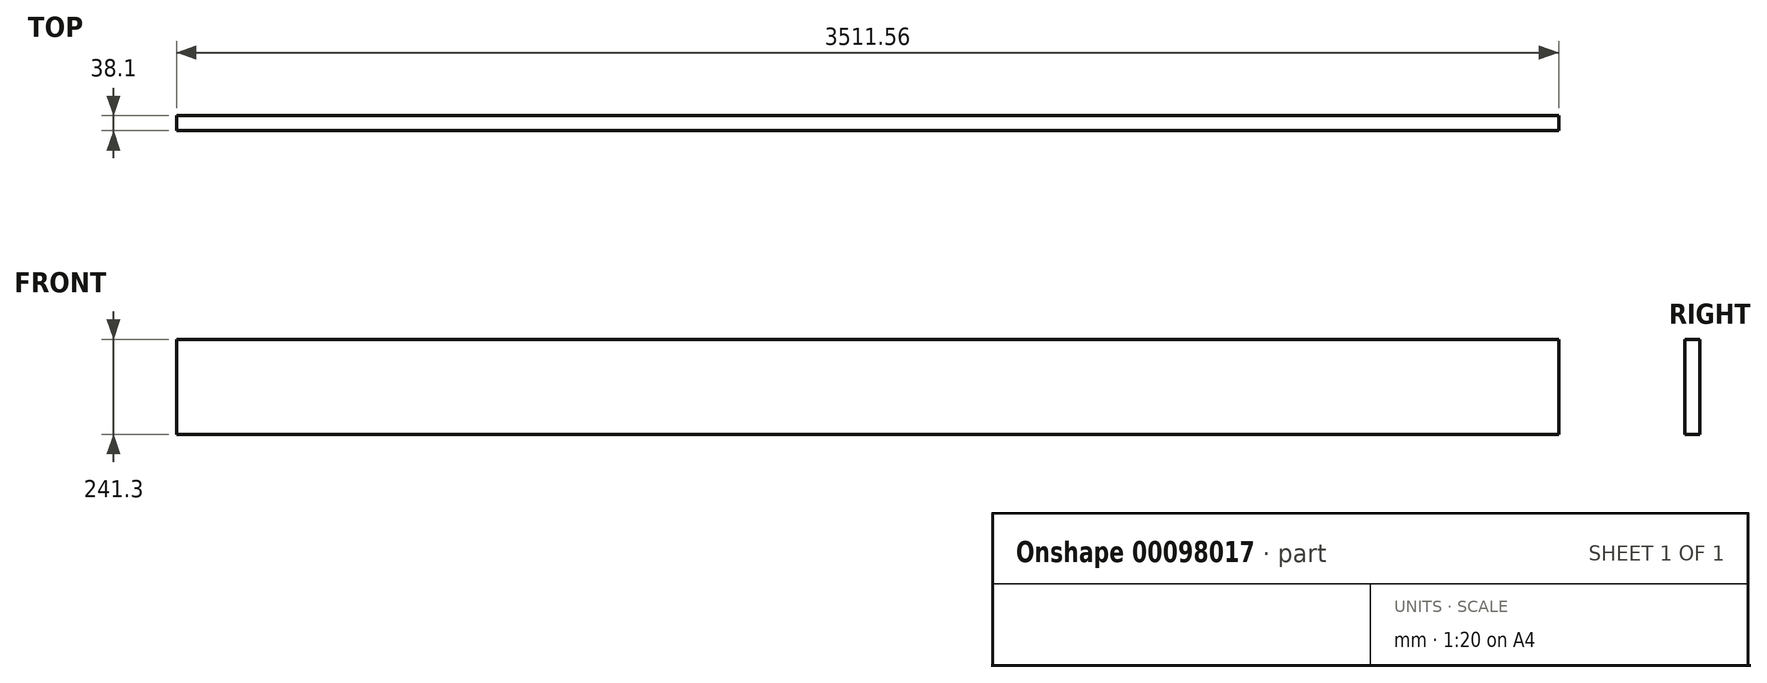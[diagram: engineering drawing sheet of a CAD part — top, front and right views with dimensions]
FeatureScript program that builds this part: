
annotation { "Feature Type Name" : "Feature", "Feature Type Description" : "" }
export const myFeature = defineFeature(function(context is Context, id is Id, definition is map)
    precondition{}
    {
        {
            var Q0;
            Q0=qCreatedBy(makeId("Front.planeOp"),FACE);
            var sketch = newSketch(context, id + "F0", { "sketchPlane" : qUnion([Q0])});
            skLineSegment(sketch, "E0.bottom", {"start": v(1755.78, 120.65) * mm, "end": v(-1755.78, 120.65) * mm});
            skLineSegment(sketch, "E0.top", {"start": v(1755.78, -120.65) * mm, "end": v(-1755.78, -120.65) * mm});
            skLineSegment(sketch, "E0.left", {"start": v(1755.78, 120.65) * mm, "end": v(1755.78, -120.65) * mm});
            skLineSegment(sketch, "E0.right", {"start": v(-1755.78, 120.65) * mm, "end": v(-1755.78, -120.65) * mm});
            skPoint(sketch, "E0.middle", {"position": v(0, 0) * mm});
            skSolve(sketch);
        }
        {
            var Q0;
            Q0=makeQuery(id+"F0.imprint","IMPRINT",FACE,{"disambiguationData":[TD([[makeQuery(id+"F0.imprint","IMPRINT",EDGE,{"derivedFrom":sQuery(id+"F0.wireOp",EDGE,"E0.bottom")}),1.0]])]});
            extrude(context, id + "F1", {"entities" : qUnion([Q0]), "depth" : 38.1 * mm});
        }
    });
